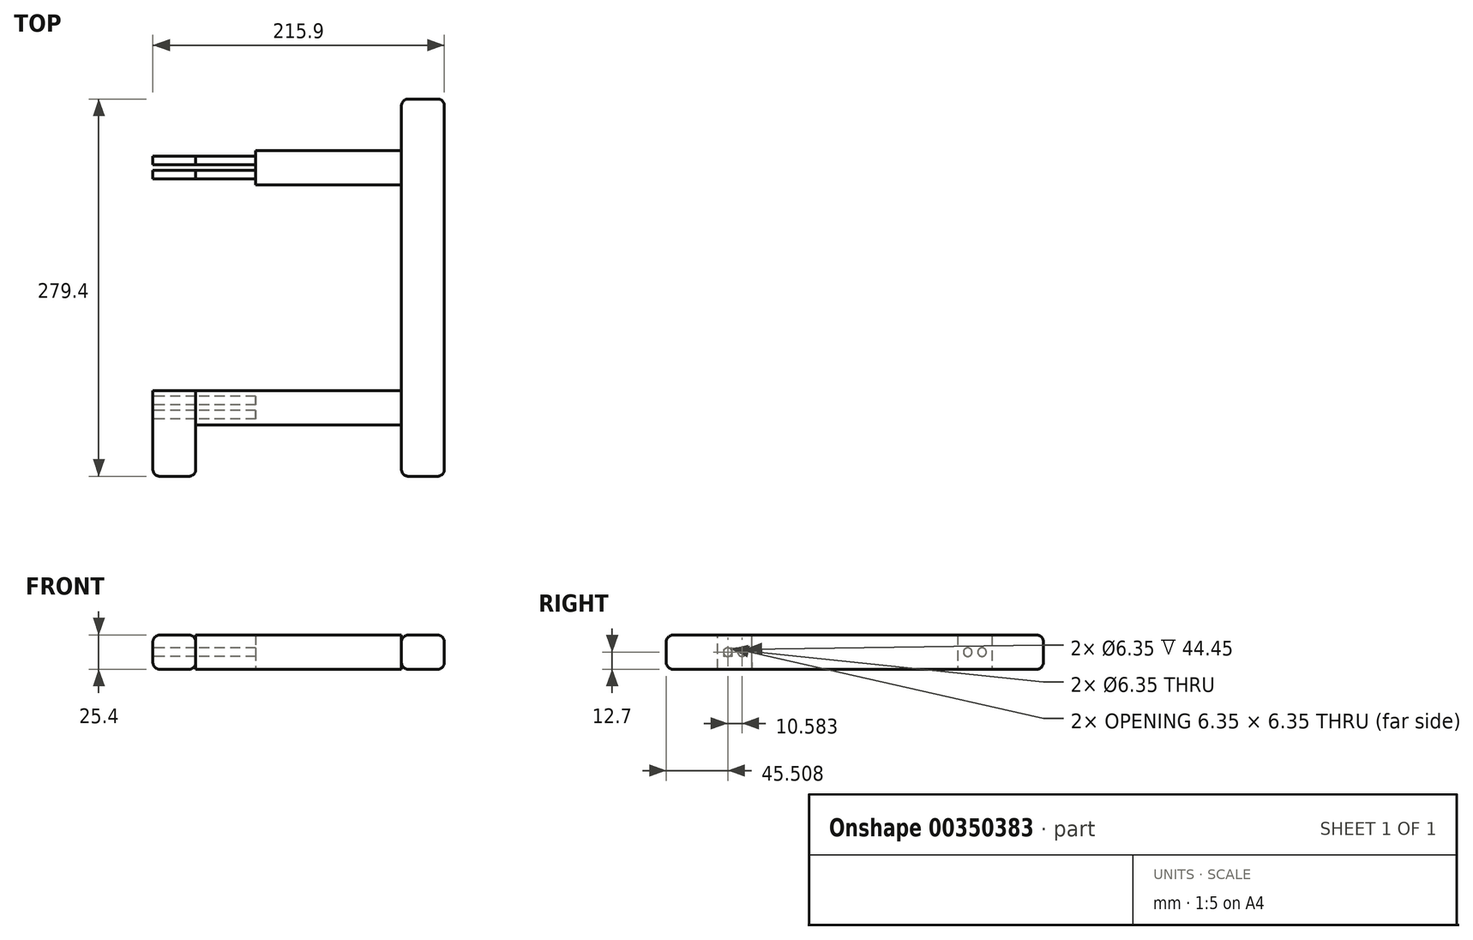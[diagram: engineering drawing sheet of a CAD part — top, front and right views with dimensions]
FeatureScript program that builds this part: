
annotation { "Feature Type Name" : "Feature", "Feature Type Description" : "" }
export const myFeature = defineFeature(function(context is Context, id is Id, definition is map)
    precondition{}
    {
        {
            var Q0;
            Q0=qCreatedBy(makeId("Top.planeOp"),FACE);
            var sketch = newSketch(context, id + "F0", { "sketchPlane" : qUnion([Q0])});
            skLineSegment(sketch, "E0.bottom", {"start": v(-107.95, 139.7) * mm, "end": v(-76.2, 139.7) * mm});
            skLineSegment(sketch, "E0.top", {"start": v(-107.95, -139.7) * mm, "end": v(-76.2, -139.7) * mm});
            skLineSegment(sketch, "E0.left", {"start": v(-107.95, 139.7) * mm, "end": v(-107.95, -139.7) * mm});
            skLineSegment(sketch, "E1", {"start": v(-76.2, 139.7) * mm, "end": v(-76.2, 0) * mm});
            skLineSegment(sketch, "E2", {"start": v(-76.2, 0) * mm, "end": v(-76.2, -139.7) * mm});
            skSolve(sketch);
        }
        {
            var Q0;
            Q0=makeQuery(id+"F0.imprint","IMPRINT",FACE,{"disambiguationData":[TD([[makeQuery(id+"F0.imprint","IMPRINT",EDGE,{"derivedFrom":sQuery(id+"F0.wireOp",EDGE,"E0.bottom")}),-1.0]])]});
            extrude(context, id + "F1", {"entities" : qUnion([Q0]), "depth" : 25.4 * mm});
        }
        {
            var Q0;
            Q0=makeQuery(id+"F1.opExtrude","SWEPT_BODY",BODY,{"disambiguationData":[OSD([sQuery(id+"F0.wireOp",EDGE,"E0.bottom"),sQuery(id+"F0.wireOp",EDGE,"E0.top"),sQuery(id+"F0.wireOp",EDGE,"E0.left"),sQuery(id+"F0.wireOp",EDGE,"E1"),sQuery(id+"F0.wireOp",EDGE,"E2")])]});
            var Q1;
            Q1=qCreatedBy(makeId("Right.planeOp"),FACE);
            mirror(context, id + "F2", {"entities" : qUnion([Q0]), "mirrorPlane" : qUnion([Q1])});
        }
        {
            var Q0;
            Q0=makeQuery(id+"F1.opExtrude","SWEPT_FACE",FACE,{"disambiguationData":[OSD([sQuery(id+"F0.wireOp",EDGE,"E1"),sQuery(id+"F0.wireOp",EDGE,"E2")])]});
            var sketch = newSketch(context, id + "F3", { "sketchPlane" : qUnion([Q0])});
            skLineSegment(sketch, "E3.bottom", {"start": v(-101.6, 25.4) * mm, "end": v(-76.2, 25.4) * mm});
            skLineSegment(sketch, "E3.top", {"start": v(-101.6, 0) * mm, "end": v(-76.2, 0) * mm});
            skLineSegment(sketch, "E3.left", {"start": v(-101.6, 25.4) * mm, "end": v(-101.6, 0) * mm});
            skLineSegment(sketch, "E3.right", {"start": v(-76.2, 25.4) * mm, "end": v(-76.2, 0) * mm});
            skSolve(sketch);
        }
        {
            var Q0;
            Q0=makeQuery(id+"F3.imprint","IMPRINT",FACE,{"disambiguationData":[TD([[makeQuery(id+"F3.imprint","IMPRINT",EDGE,{"derivedFrom":sQuery(id+"F3.wireOp",EDGE,"E3.bottom")}),1.0]])]});
            var Q1;
            Q1=makeQuery(id+"F2.opPattern","COPY",FACE,{"derivedFrom":makeQuery(id+"F1.opExtrude","SWEPT_FACE",FACE,{"disambiguationData":[OSD([sQuery(id+"F0.wireOp",EDGE,"E1"),sQuery(id+"F0.wireOp",EDGE,"E2")])]}),"instanceName":"1"});
            extrude(context, id + "F4", {"entities" : qUnion([Q0]), "endBound" : BoundingType.UP_TO_SURFACE, "endBoundEntityFace" : qUnion([Q1]), "depth" : 25.4 * mm});
        }
        {
            var Q0;
            Q0=makeQuery(id+"F4.opExtrude","SWEPT_BODY",BODY,{"disambiguationData":[OSD([sQuery(id+"F3.wireOp",EDGE,"E3.bottom"),sQuery(id+"F3.wireOp",EDGE,"E3.top"),sQuery(id+"F3.wireOp",EDGE,"E3.left"),sQuery(id+"F3.wireOp",EDGE,"E3.right")])]});
            var Q1;
            Q1=qCreatedBy(makeId("Front.planeOp"),FACE);
            mirror(context, id + "F5", {"entities" : qUnion([Q0]), "mirrorPlane" : qUnion([Q1])});
        }
        {
            var Q0;
            Q0=makeQuery(id+"F1.opExtrude","SWEPT_FACE",FACE,{"disambiguationData":[OSD([sQuery(id+"F0.wireOp",EDGE,"E0.left")])]});
            var sketch = newSketch(context, id + "F6", { "sketchPlane" : qUnion([Q0])});
            skLineSegment(sketch, "E4.0", {"start": v(76.2, 25.4) * mm, "end": v(76.2, 0) * mm});
            skPoint(sketch, "E5.endSnap0", {"position": v(76.2, 12.7) * mm});
            skCircle(sketch, "E6", {"center": v(94.2, 12.7) * mm, "radius": 3.17 * mm});
            skCircle(sketch, "E7", {"center": v(83.6, 12.7) * mm, "radius": 3.17 * mm});
            skLineSegment(sketch, "E8.0.1", {"start": v(101.6, 0) * mm, "end": v(101.6, 25.4) * mm});
            skLineSegment(sketch, "E8.0.3", {"start": v(101.6, 25.4) * mm, "end": v(101.6, 0) * mm});
            skPoint(sketch, "E9", {"position": v(101.6, 12.7) * mm});
            skLineSegment(sketch, "E10", {"start": v(101.6, 12.7) * mm, "end": v(76.2, 12.7) * mm, "construction": true});
            skLineSegment(sketch, "E11", {"start": v(101.6, 12.7) * mm, "end": v(97.37, 12.7) * mm, "construction": true});
            skLineSegment(sketch, "E12", {"start": v(91.02, 12.7) * mm, "end": v(86.78, 12.7) * mm, "construction": true});
            skLineSegment(sketch, "E13", {"start": v(80.43, 12.7) * mm, "end": v(76.2, 12.7) * mm, "construction": true});
            skCircle(sketch, "E14.MirrorC", {"center": v(-94.2, 12.7) * mm, "radius": 3.17 * mm});
            skCircle(sketch, "E15.MirrorC", {"center": v(-83.6, 12.7) * mm, "radius": 3.17 * mm});
            skSolve(sketch);
        }
        {
            var Q0;
            Q0=makeQuery(id+"F6.imprint","IMPRINT",FACE,{"disambiguationData":[TD([[makeQuery(id+"F6.imprint","IMPRINT",EDGE,{"derivedFrom":sQuery(id+"F6.wireOp",EDGE,"E6")}),1.0]])]});
            var Q1;
            Q1=makeQuery(id+"F6.imprint","IMPRINT",FACE,{"disambiguationData":[TD([[makeQuery(id+"F6.imprint","IMPRINT",EDGE,{"derivedFrom":sQuery(id+"F6.wireOp",EDGE,"E7")}),1.0]])]});
            var Q2;
            Q2=makeQuery(id+"F6.imprint","IMPRINT",FACE,{"disambiguationData":[TD([[makeQuery(id+"F6.imprint","IMPRINT",EDGE,{"derivedFrom":sQuery(id+"F6.wireOp",EDGE,"E15.MirrorC")}),-1.0]])]});
            var Q3;
            Q3=makeQuery(id+"F6.imprint","IMPRINT",FACE,{"disambiguationData":[TD([[makeQuery(id+"F6.imprint","IMPRINT",EDGE,{"derivedFrom":sQuery(id+"F6.wireOp",EDGE,"E14.MirrorC")}),-1.0]])]});
            extrude(context, id + "F7", {"entities" : qUnion([Q0, Q1, Q2, Q3]), "operationType" : NewBodyOperationType.REMOVE, "oppositeDirection" : true, "depth" : 76.2 * mm});
        }
        {
            var Q0;
            Q0=makeQuery(id+"F1.opExtrude","SWEPT_EDGE",EDGE,{"disambiguationData":[OSD([sQuery(id+"F0.wireOp",EDGE,"E0.top"),sQuery(id+"F0.wireOp",EDGE,"E0.left")])]});
            var Q1;
            Q1=makeQuery(id+"F1.opExtrude","SWEPT_EDGE",EDGE,{"disambiguationData":[OSD([sQuery(id+"F0.wireOp",EDGE,"E0.top"),sQuery(id+"F0.wireOp",EDGE,"E2")])]});
            var Q2;
            Q2=makeQuery(id+"F2.opPattern","COPY",EDGE,{"derivedFrom":makeQuery(id+"F1.opExtrude","SWEPT_EDGE",EDGE,{"disambiguationData":[OSD([sQuery(id+"F0.wireOp",EDGE,"E0.top"),sQuery(id+"F0.wireOp",EDGE,"E2")])]}),"instanceName":"1"});
            var Q3;
            Q3=makeQuery(id+"F2.opPattern","COPY",EDGE,{"derivedFrom":makeQuery(id+"F1.opExtrude","SWEPT_EDGE",EDGE,{"disambiguationData":[OSD([sQuery(id+"F0.wireOp",EDGE,"E0.top"),sQuery(id+"F0.wireOp",EDGE,"E0.left")])]}),"instanceName":"1"});
            var Q4;
            Q4=makeQuery(id+"F2.opPattern","COPY",EDGE,{"derivedFrom":makeQuery(id+"F1.opExtrude","SWEPT_EDGE",EDGE,{"disambiguationData":[OSD([sQuery(id+"F0.wireOp",EDGE,"E0.bottom"),sQuery(id+"F0.wireOp",EDGE,"E0.left")])]}),"instanceName":"1"});
            var Q5;
            Q5=makeQuery(id+"F2.opPattern","COPY",EDGE,{"derivedFrom":makeQuery(id+"F1.opExtrude","SWEPT_EDGE",EDGE,{"disambiguationData":[OSD([sQuery(id+"F0.wireOp",EDGE,"E0.bottom"),sQuery(id+"F0.wireOp",EDGE,"E1")])]}),"instanceName":"1"});
            var Q6;
            Q6=makeQuery(id+"F1.opExtrude","SWEPT_EDGE",EDGE,{"disambiguationData":[OSD([sQuery(id+"F0.wireOp",EDGE,"E0.bottom"),sQuery(id+"F0.wireOp",EDGE,"E1")])]});
            var Q7;
            Q7=makeQuery(id+"F1.opExtrude","SWEPT_EDGE",EDGE,{"disambiguationData":[OSD([sQuery(id+"F0.wireOp",EDGE,"E0.bottom"),sQuery(id+"F0.wireOp",EDGE,"E0.left")])]});
            fillet(context, id + "F8", {"entities" : qUnion([Q0, Q1, Q2, Q3, Q4, Q5, Q6, Q7]), "radius" : 5.08 * mm, "tangentPropagation" : true, "allowEdgeOverflow" : false});
        }
        {
            var Q0;
            Q0=makeQuery(id+"F1.opExtrude","CAP_EDGE",EDGE,{"disambiguationData":[OSD([sQuery(id+"F0.wireOp",EDGE,"E0.left")])],"isStart":false});
            var Q1;
            Q1=makeQuery(id+"F2.opPattern","COPY",EDGE,{"derivedFrom":makeQuery(id+"F1.opExtrude","CAP_EDGE",EDGE,{"disambiguationData":[OSD([sQuery(id+"F0.wireOp",EDGE,"E0.left")])],"isStart":false}),"instanceName":"1"});
            var Q2;
            Q2=makeQuery(id+"F2.opPattern","COPY",EDGE,{"derivedFrom":makeQuery(id+"F1.opExtrude","CAP_EDGE",EDGE,{"disambiguationData":[OSD([sQuery(id+"F0.wireOp",EDGE,"E0.left")])],"isStart":true}),"instanceName":"1"});
            var Q3;
            Q3=makeQuery(id+"F1.opExtrude","CAP_EDGE",EDGE,{"disambiguationData":[OSD([sQuery(id+"F0.wireOp",EDGE,"E0.left")])],"isStart":true});
            fillet(context, id + "F9", {"entities" : qUnion([Q0, Q1, Q2, Q3]), "radius" : 5.08 * mm, "tangentPropagation" : true, "allowEdgeOverflow" : false});
        }
    });
